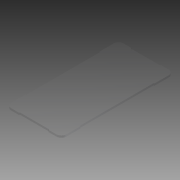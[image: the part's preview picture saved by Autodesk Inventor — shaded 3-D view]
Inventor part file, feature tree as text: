
AUTODESK INVENTOR PART (.ipt)
format: ipt  version: 2015 (Build 190159000, 159)  size: 130,048 bytes
history: native  units: mm
features: extrude x2, fillet x2
ambient origin geometry x8: Origin, YZ Plane, XZ Plane, XY Plane, X Axis, Y Axis, Z Axis, Center Point
bodies: Solid1 (feature_tree)
feature tree (4):
  extrude  "Extrusión1"  Depth=85.8mm
  extrude  "Extrusión3"  Depth=174.8mm
  fillet  "Empalme2"  Radius=3.0mm
  fillet  "Empalme3"  Radius=30.0mm
